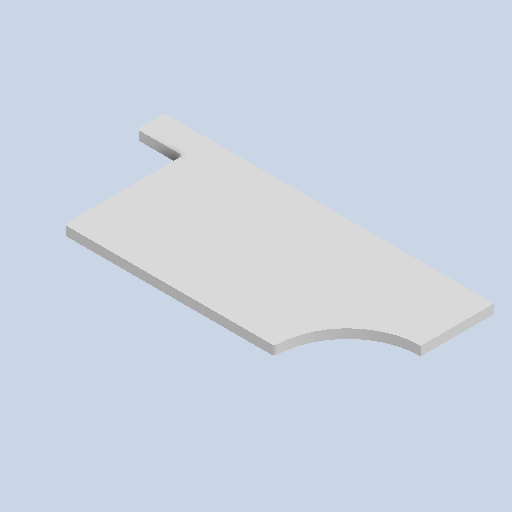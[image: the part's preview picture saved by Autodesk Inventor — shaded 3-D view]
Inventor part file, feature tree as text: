
AUTODESK INVENTOR PART (.ipt)
format: ipt  version: 2025.2 (Build 292293000, 293)  size: 178,688 bytes
history: native  units: mm
features: sketch x2, other x1, extrude x1
ambient origin geometry x8: Origin, YZ Plane, XZ Plane, XY Plane, X Axis, Y Axis, Z Axis, Center Point
bodies: Body1 (feature_tree)
feature tree (4):
  other  "Sólido1"
  sketch  "Esboço1"  dims[d0=800.0mm d1=1800.0mm]
  sketch  "Esboço3"  dims[d3=650.0mm d5=15.0mm d6=800.0mm d7=1800.0mm d9=250.0mm d11=800.0mm d13=400.0mm d14=400.0mm d15=400.0mm d16=1800.0mm d17=800.0mm d19=200.0mm d20=50.0mm d21=800.0mm d22=50.0mm d23=0.0mm d24=0.5mm d25=0.872665mm]
  extrude  "Extrusão1"  Depth=1800.0mm
